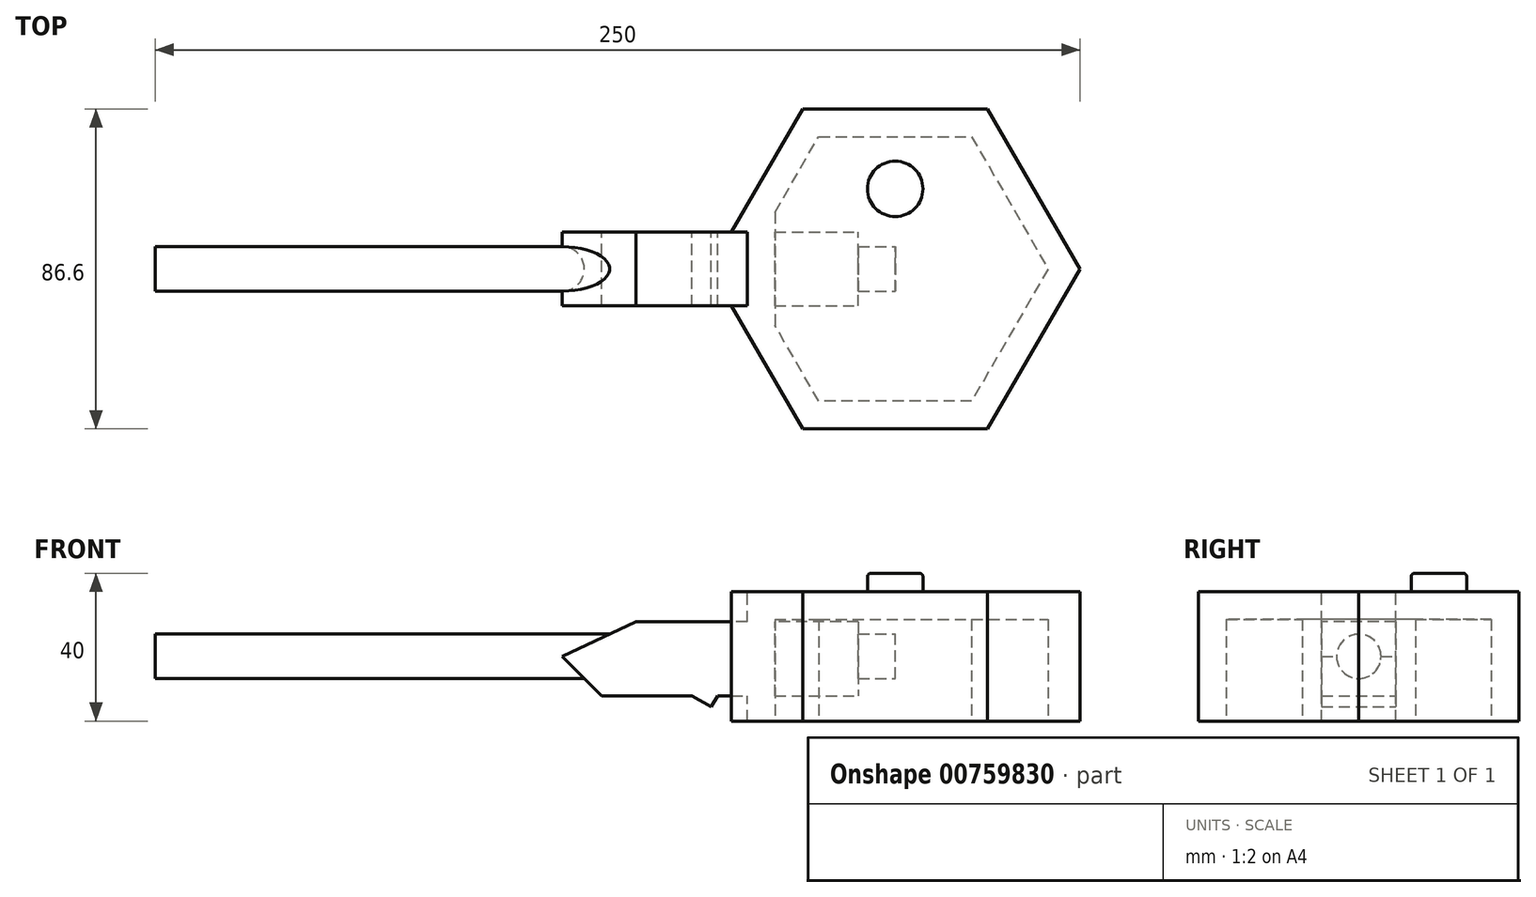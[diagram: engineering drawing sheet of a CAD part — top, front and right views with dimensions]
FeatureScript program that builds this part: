
annotation { "Feature Type Name" : "Feature", "Feature Type Description" : "" }
export const myFeature = defineFeature(function(context is Context, id is Id, definition is map)
    precondition{}
    {
        {
            var Q0;
            Q0=qCreatedBy(makeId("Top.planeOp"),FACE);
            var sketch = newSketch(context, id + "F0", { "sketchPlane" : qUnion([Q0])});
            skCircle(sketch, "E0.cCircle", {"center": v(0, 0) * mm, "radius": 43.3 * mm, "construction": true});
            skLineSegment(sketch, "E0.0", {"start": v(-25, 43.3) * mm, "end": v(25, 43.3) * mm});
            skLineSegment(sketch, "E0.1", {"start": v(25, 43.3) * mm, "end": v(50, 0) * mm});
            skLineSegment(sketch, "E0.2", {"start": v(50, 0) * mm, "end": v(25, -43.3) * mm});
            skLineSegment(sketch, "E0.3", {"start": v(25, -43.3) * mm, "end": v(-25, -43.3) * mm});
            skLineSegment(sketch, "E0.4", {"start": v(-25, -43.3) * mm, "end": v(-50, 0) * mm});
            skLineSegment(sketch, "E0.5", {"start": v(-50, 0) * mm, "end": v(-25, 43.3) * mm});
            skPoint(sketch, "E0.0.midPoint", {"position": v(0, 43.3) * mm});
            skSolve(sketch);
        }
        {
            var Q0;
            Q0 = qSketchRegion(id + "F0", true);
            extrude(context, id + "F1", {"entities" : qUnion([Q0]), "depth" : 35 * mm, "offsetDistance" : 25 * mm});
        }
        {
            var Q0;
            Q0=makeQuery(id+"F1.opExtrude","CAP_FACE",FACE,{"disambiguationData":[OSD([sQuery(id+"F0.wireOp",EDGE,"E0.0"),sQuery(id+"F0.wireOp",EDGE,"E0.1"),sQuery(id+"F0.wireOp",EDGE,"E0.2"),sQuery(id+"F0.wireOp",EDGE,"E0.3"),sQuery(id+"F0.wireOp",EDGE,"E0.4"),sQuery(id+"F0.wireOp",EDGE,"E0.5")])],"isStart":false});
            var sketch = newSketch(context, id + "F2", { "sketchPlane" : qUnion([Q0])});
            skCircle(sketch, "E1", {"center": v(0, 21.65) * mm, "radius": 7.5 * mm});
            skLineSegment(sketch, "E2", {"start": v(0, 43.3) * mm, "end": v(0, 0) * mm, "construction": true});
            skSolve(sketch);
        }
        {
            var Q0;
            Q0 = qSketchRegion(id + "F2", true);
            extrude(context, id + "F3", {"entities" : qUnion([Q0]), "operationType" : NewBodyOperationType.ADD, "depth" : 5 * mm, "offsetDistance" : 25 * mm});
        }
        {
            var Q0;
            Q0=makeQuery(id+"F3.opExtrude","CAP_EDGE",EDGE,{"disambiguationData":[OSD([sQuery(id+"F2.wireOp",EDGE,"E1")])],"isStart":false});
            fillet(context, id + "F4", {"entities" : qUnion([Q0]), "radius" : 1 * mm, "tangentPropagation" : true, "allowEdgeOverflow" : false});
        }
        {
            var Q0;
            Q0=makeQuery(id+"F1.opExtrude","CAP_FACE",FACE,{"disambiguationData":[OSD([sQuery(id+"F0.wireOp",EDGE,"E0.0"),sQuery(id+"F0.wireOp",EDGE,"E0.1"),sQuery(id+"F0.wireOp",EDGE,"E0.2"),sQuery(id+"F0.wireOp",EDGE,"E0.3"),sQuery(id+"F0.wireOp",EDGE,"E0.4"),sQuery(id+"F0.wireOp",EDGE,"E0.5")])],"isStart":false});
            var sketch = newSketch(context, id + "F5", { "sketchPlane" : qUnion([Q0])});
            skLineSegment(sketch, "E3.bottom", {"start": v(-60, 10) * mm, "end": v(-40, 10) * mm});
            skLineSegment(sketch, "E3.top", {"start": v(-60, -10) * mm, "end": v(-40, -10) * mm});
            skLineSegment(sketch, "E3.left", {"start": v(-60, 10) * mm, "end": v(-60, -10) * mm});
            skLineSegment(sketch, "E3.right", {"start": v(-40, 10) * mm, "end": v(-40, -10) * mm});
            skLineSegment(sketch, "E4", {"start": v(-60, -10) * mm, "end": v(-40, 10) * mm, "construction": true});
            skSolve(sketch);
        }
        {
            var Q0;
            Q0 = qSketchRegion(id + "F5", true);
            extrude(context, id + "F6", {"entities" : qUnion([Q0]), "operationType" : NewBodyOperationType.REMOVE, "endBound" : BoundingType.THROUGH_ALL, "oppositeDirection" : true, "depth" : 25 * mm, "offsetDistance" : 25 * mm});
        }
        {
            var Q0;
            Q0=makeQuery(id+"F1.opExtrude","CAP_FACE",FACE,{"disambiguationData":[OSD([sQuery(id+"F0.wireOp",EDGE,"E0.0"),sQuery(id+"F0.wireOp",EDGE,"E0.1"),sQuery(id+"F0.wireOp",EDGE,"E0.2"),sQuery(id+"F0.wireOp",EDGE,"E0.3"),sQuery(id+"F0.wireOp",EDGE,"E0.4"),sQuery(id+"F0.wireOp",EDGE,"E0.5")])],"isStart":true});
            shell(context, id + "F7", {"entities" : qUnion([Q0]), "thickness" : 7.5 * mm});
        }
        {
            var Q0;
            Q0=qCreatedBy(makeId("Front.planeOp"),FACE);
            var sketch = newSketch(context, id + "F8", { "sketchPlane" : qUnion([Q0])});
            skLineSegment(sketch, "E5", {"start": v(-10, 26.83) * mm, "end": v(-70, 26.83) * mm});
            skLineSegment(sketch, "E6", {"start": v(-70, 26.83) * mm, "end": v(-90, 17.5) * mm});
            skLineSegment(sketch, "E7", {"start": v(-90, 17.5) * mm, "end": v(-79.33, 6.83) * mm});
            skLineSegment(sketch, "E8", {"start": v(-79.33, 6.83) * mm, "end": v(-54.93, 6.83) * mm});
            skLineSegment(sketch, "E9", {"start": v(-54.93, 6.83) * mm, "end": v(-49.73, 3.83) * mm});
            skLineSegment(sketch, "E10", {"start": v(-49.73, 3.83) * mm, "end": v(-48, 6.83) * mm});
            skLineSegment(sketch, "E11", {"start": v(-48, 6.83) * mm, "end": v(-10, 6.83) * mm});
            skLineSegment(sketch, "E12", {"start": v(61.47, 17.5) * mm, "end": v(-273.35, 17.5) * mm, "construction": true});
            skLineSegment(sketch, "E13", {"start": v(-10, 26.83) * mm, "end": v(-10, 6.83) * mm});
            skLineSegment(sketch, "E14.0", {"start": v(-40, 0) * mm, "end": v(-40, 35) * mm, "construction": true});
            skLineSegment(sketch, "E15", {"start": v(-40, 26.83) * mm, "end": v(-40, 6.83) * mm, "construction": true});
            skSolve(sketch);
        }
        {
            var Q0;
            Q0=qCreatedBy(makeId("Right.planeOp"),FACE);
            var sketch = newSketch(context, id + "F9", { "sketchPlane" : qUnion([Q0])});
            skCircle(sketch, "E16", {"center": v(0, 17.5) * mm, "radius": 6 * mm});
            skSolve(sketch);
        }
        {
            var Q0;
            Q0 = qSketchRegion(id + "F8", true);
            extrude(context, id + "F10", {"entities" : qUnion([Q0]), "operationType" : NewBodyOperationType.ADD, "endBound" : BoundingType.SYMMETRIC, "depth" : 20 * mm, "offsetDistance" : 25 * mm});
        }
        {
            var Q0;
            Q0 = qSketchRegion(id + "F9", true);
            extrude(context, id + "F11", {"entities" : qUnion([Q0]), "operationType" : NewBodyOperationType.ADD, "oppositeDirection" : true, "depth" : 200 * mm, "offsetDistance" : 25 * mm});
        }
    });
